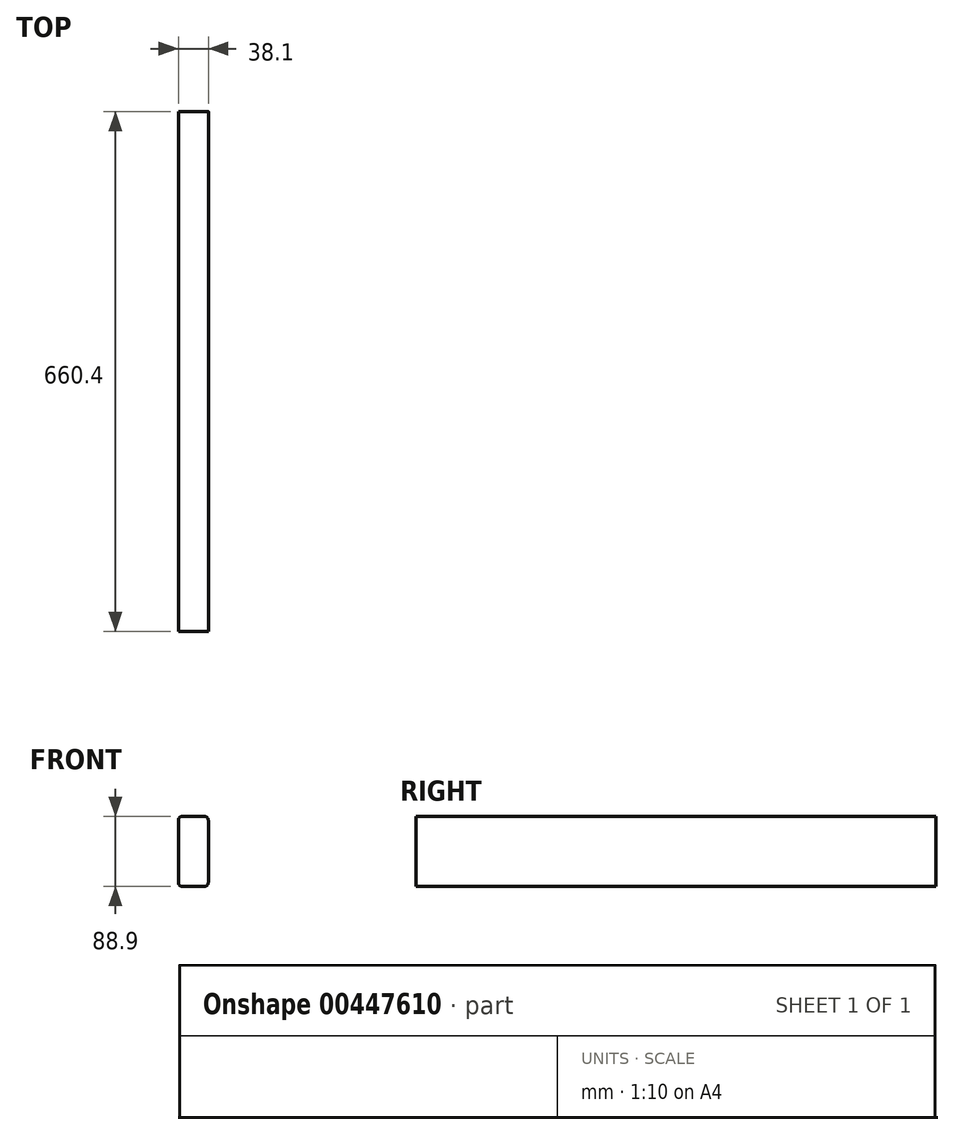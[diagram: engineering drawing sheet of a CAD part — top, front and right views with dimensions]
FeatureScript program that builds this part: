
annotation { "Feature Type Name" : "Feature", "Feature Type Description" : "" }
export const myFeature = defineFeature(function(context is Context, id is Id, definition is map)
    precondition{}
    {
        {
            var Q0;
            Q0=qCreatedBy(makeId("Front.planeOp"),FACE);
            var sketch = newSketch(context, id + "F0", { "sketchPlane" : qUnion([Q0])});
            skLineSegment(sketch, "E0.bottom", {"start": v(0, 0) * mm, "end": v(38.1, 0) * mm});
            skLineSegment(sketch, "E0.top", {"start": v(0, 88.9) * mm, "end": v(38.1, 88.9) * mm});
            skLineSegment(sketch, "E0.left", {"start": v(0, 0) * mm, "end": v(0, 88.9) * mm});
            skLineSegment(sketch, "E0.right", {"start": v(38.1, 0) * mm, "end": v(38.1, 88.9) * mm});
            skSolve(sketch);
        }
        {
            var Q0;
            Q0 = qSketchRegion(id + "F0", true);
            extrude(context, id + "F1", {"entities" : qUnion([Q0]), "depth" : 660.4 * mm});
        }
        {
            var Q0;
            Q0=makeQuery(id+"F1.opExtrude","SWEPT_EDGE",EDGE,{"disambiguationData":[OSD([sQuery(id+"F0.wireOp",EDGE,"E0.top"),sQuery(id+"F0.wireOp",EDGE,"E0.right")])]});
            var Q1;
            Q1=makeQuery(id+"F1.opExtrude","SWEPT_EDGE",EDGE,{"disambiguationData":[OSD([sQuery(id+"F0.wireOp",EDGE,"E0.top"),sQuery(id+"F0.wireOp",EDGE,"E0.left")])]});
            var Q2;
            Q2=makeQuery(id+"F1.opExtrude","SWEPT_EDGE",EDGE,{"disambiguationData":[OSD([sQuery(id+"F0.wireOp",EDGE,"E0.bottom"),sQuery(id+"F0.wireOp",EDGE,"E0.right")])]});
            var Q3;
            Q3=makeQuery(id+"F1.opExtrude","SWEPT_EDGE",EDGE,{"disambiguationData":[OSD([sQuery(id+"F0.wireOp",EDGE,"E0.bottom"),sQuery(id+"F0.wireOp",EDGE,"E0.left")])]});
            fillet(context, id + "F2", {"entities" : qUnion([Q0, Q1, Q2, Q3]), "radius" : 5.08 * mm, "tangentPropagation" : true, "allowEdgeOverflow" : false});
        }
    });
